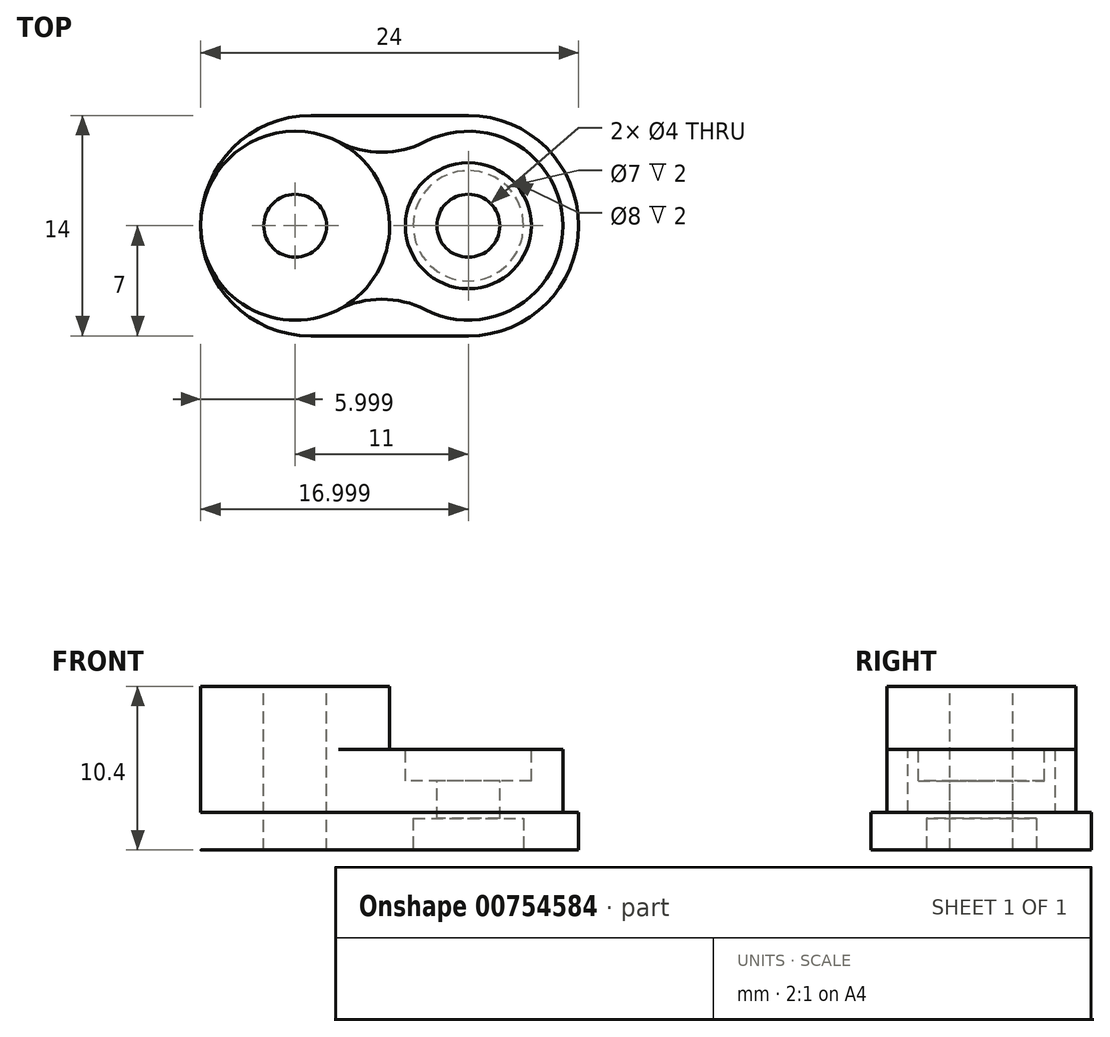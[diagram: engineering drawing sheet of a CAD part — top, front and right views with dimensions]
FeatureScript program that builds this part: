
annotation { "Feature Type Name" : "Feature", "Feature Type Description" : "" }
export const myFeature = defineFeature(function(context is Context, id is Id, definition is map)
    precondition{}
    {
        {
            var Q0;
            Q0=qCreatedBy(makeId("Top.planeOp"),FACE);
            var sketch = newSketch(context, id + "F0", { "sketchPlane" : qUnion([Q0])});
            skLineSegment(sketch, "E0.bottom", {"start": v(-15.26, 0) * mm, "end": v(8.74, 0) * mm});
            skLineSegment(sketch, "E0.top", {"start": v(-15.26, 14) * mm, "end": v(8.74, 14) * mm});
            skLineSegment(sketch, "E0.left", {"start": v(-15.26, 0) * mm, "end": v(-15.26, 14) * mm});
            skLineSegment(sketch, "E0.right", {"start": v(8.74, 0) * mm, "end": v(8.74, 14) * mm});
            skSolve(sketch);
        }
        {
            var Q0;
            Q0=makeQuery(id+"F0.imprint","IMPRINT",FACE,{"disambiguationData":[TD([[makeQuery(id+"F0.imprint","IMPRINT",EDGE,{"derivedFrom":sQuery(id+"F0.wireOp",EDGE,"E0.bottom")}),1.0]])]});
            extrude(context, id + "F1", {"entities" : qUnion([Q0]), "depth" : 2.4 * mm, "offsetDistance" : 25 * mm});
        }
        {
            var Q0;
            Q0=makeQuery(id+"F1.opExtrude","CAP_FACE",FACE,{"disambiguationData":[OSD([sQuery(id+"F0.wireOp",EDGE,"E0.bottom"),sQuery(id+"F0.wireOp",EDGE,"E0.top"),sQuery(id+"F0.wireOp",EDGE,"E0.left"),sQuery(id+"F0.wireOp",EDGE,"E0.right")])],"isStart":false});
            var sketch = newSketch(context, id + "F2", { "sketchPlane" : qUnion([Q0])});
            skCircle(sketch, "E1", {"center": v(-9.26, 7) * mm, "radius": 2 * mm});
            skSolve(sketch);
        }
        {
            var Q0;
            Q0=makeQuery(id+"F2.imprint","IMPRINT",FACE,{"disambiguationData":[TD([[makeQuery(id+"F2.imprint","IMPRINT",EDGE,{"derivedFrom":sQuery(id+"F2.wireOp",EDGE,"E1")}),-1.0]])]});
            var sketch = newSketch(context, id + "F3", { "sketchPlane" : qUnion([Q0])});
            skCircle(sketch, "E2", {"center": v(-9.26, 7) * mm, "radius": 6 * mm});
            skSolve(sketch);
        }
        {
            var Q0;
            Q0 = qSketchRegion(id + "F3", true);
            extrude(context, id + "F4", {"entities" : qUnion([Q0]), "operationType" : NewBodyOperationType.ADD, "depth" : 8 * mm, "offsetDistance" : 25 * mm});
        }
        {
            var Q0;
            Q0=makeQuery(id+"F2.imprint","IMPRINT",FACE,{"disambiguationData":[TD([[makeQuery(id+"F2.imprint","IMPRINT",EDGE,{"derivedFrom":sQuery(id+"F2.wireOp",EDGE,"E1")}),-1.0]])]});
            var sketch = newSketch(context, id + "F5", { "sketchPlane" : qUnion([Q0])});
            skCircle(sketch, "E3", {"center": v(1.74, 7) * mm, "radius": 6 * mm});
            skSolve(sketch);
        }
        {
            var Q0;
            Q0 = qSketchRegion(id + "F5", true);
            extrude(context, id + "F6", {"entities" : qUnion([Q0]), "operationType" : NewBodyOperationType.ADD, "depth" : 4 * mm, "offsetDistance" : 25 * mm});
        }
        {
            var Q0;
            Q0 = qSketchRegion(id + "F2", true);
            extrude(context, id + "F7", {"entities" : qUnion([Q0]), "operationType" : NewBodyOperationType.REMOVE, "endBound" : BoundingType.THROUGH_ALL, "oppositeDirection" : true, "depth" : 25 * mm, "offsetDistance" : 25 * mm, "hasSecondDirection" : true, "secondDirectionBound" : SecondDirectionBoundingType.THROUGH_ALL, "secondDirectionOppositeDirection" : false, "secondDirectionDepth" : 25 * mm});
        }
        {
            var Q0;
            Q0=makeQuery(id+"F6.opExtrude","CAP_FACE",FACE,{"disambiguationData":[OSD([sQuery(id+"F5.wireOp",EDGE,"E3")])],"isStart":false});
            var sketch = newSketch(context, id + "F8", { "sketchPlane" : qUnion([Q0])});
            skCircle(sketch, "E4", {"center": v(1.74, 7) * mm, "radius": 2 * mm});
            skSolve(sketch);
        }
        {
            var Q0;
            Q0 = qSketchRegion(id + "F8", true);
            extrude(context, id + "F9", {"entities" : qUnion([Q0]), "operationType" : NewBodyOperationType.REMOVE, "endBound" : BoundingType.THROUGH_ALL, "oppositeDirection" : true, "depth" : 25 * mm, "offsetDistance" : 25 * mm});
        }
        {
            var Q0;
            Q0=makeQuery(id+"F1.opExtrude","CAP_FACE",FACE,{"disambiguationData":[OSD([sQuery(id+"F0.wireOp",EDGE,"E0.bottom"),sQuery(id+"F0.wireOp",EDGE,"E0.top"),sQuery(id+"F0.wireOp",EDGE,"E0.left"),sQuery(id+"F0.wireOp",EDGE,"E0.right")])],"isStart":true});
            var sketch = newSketch(context, id + "F10", { "sketchPlane" : qUnion([Q0])});
            skCircle(sketch, "E5", {"center": v(1.74, -7) * mm, "radius": 3.5 * mm});
            skSolve(sketch);
        }
        {
            var Q0;
            Q0 = qSketchRegion(id + "F10", true);
            extrude(context, id + "F11", {"entities" : qUnion([Q0]), "operationType" : NewBodyOperationType.REMOVE, "oppositeDirection" : true, "depth" : 2 * mm, "offsetDistance" : 25 * mm});
        }
        {
            var Q0;
            Q0=makeQuery(id+"F6.opExtrude","CAP_FACE",FACE,{"disambiguationData":[OSD([sQuery(id+"F5.wireOp",EDGE,"E3")])],"isStart":false});
            var sketch = newSketch(context, id + "F12", { "sketchPlane" : qUnion([Q0])});
            skCircle(sketch, "E6", {"center": v(1.74, 7) * mm, "radius": 4 * mm});
            skSolve(sketch);
        }
        {
            var Q0;
            Q0 = qSketchRegion(id + "F12", true);
            extrude(context, id + "F13", {"entities" : qUnion([Q0]), "operationType" : NewBodyOperationType.REMOVE, "oppositeDirection" : true, "depth" : 2 * mm, "offsetDistance" : 25 * mm});
        }
        {
            var Q0;
            Q0=makeQuery(id+"F1.opExtrude","SWEPT_EDGE",EDGE,{"disambiguationData":[OSD([sQuery(id+"F0.wireOp",EDGE,"E0.top"),sQuery(id+"F0.wireOp",EDGE,"E0.left")])]});
            var Q1;
            Q1=makeQuery(id+"F1.opExtrude","SWEPT_EDGE",EDGE,{"disambiguationData":[OSD([sQuery(id+"F0.wireOp",EDGE,"E0.bottom"),sQuery(id+"F0.wireOp",EDGE,"E0.left")])]});
            var Q2;
            Q2=makeQuery(id+"F1.opExtrude","SWEPT_EDGE",EDGE,{"disambiguationData":[OSD([sQuery(id+"F0.wireOp",EDGE,"E0.bottom"),sQuery(id+"F0.wireOp",EDGE,"E0.right")])]});
            var Q3;
            Q3=makeQuery(id+"F1.opExtrude","SWEPT_EDGE",EDGE,{"disambiguationData":[OSD([sQuery(id+"F0.wireOp",EDGE,"E0.top"),sQuery(id+"F0.wireOp",EDGE,"E0.right")])]});
            fillet(context, id + "F14", {"entities" : qUnion([Q0, Q1, Q2, Q3]), "radius" : 7 * mm, "tangentPropagation" : true, "allowEdgeOverflow" : false});
        }
        {
            var Q0;
            Q0=makeQuery(id+"F6.boolean.opBoolean","INTERSECT",EDGE,{"disambiguationData":[OD(0.0)],"derivedFrom":[makeQuery(id+"F4.opExtrude","SWEPT_FACE",FACE,{"disambiguationData":[OSD([sQuery(id+"F3.wireOp",EDGE,"E2")])]}),makeQuery(id+"F6.opExtrude","SWEPT_FACE",FACE,{"disambiguationData":[OSD([sQuery(id+"F5.wireOp",EDGE,"E3")])]})]});
            var Q1;
            Q1=makeQuery(id+"F6.boolean.opBoolean","INTERSECT",EDGE,{"disambiguationData":[OD(1.0)],"derivedFrom":[makeQuery(id+"F4.opExtrude","SWEPT_FACE",FACE,{"disambiguationData":[OSD([sQuery(id+"F3.wireOp",EDGE,"E2")])]}),makeQuery(id+"F6.opExtrude","SWEPT_FACE",FACE,{"disambiguationData":[OSD([sQuery(id+"F5.wireOp",EDGE,"E3")])]})]});
            fillet(context, id + "F15", {"entities" : qUnion([Q0, Q1]), "radius" : 6 * mm, "tangentPropagation" : true, "allowEdgeOverflow" : false});
        }
    });
